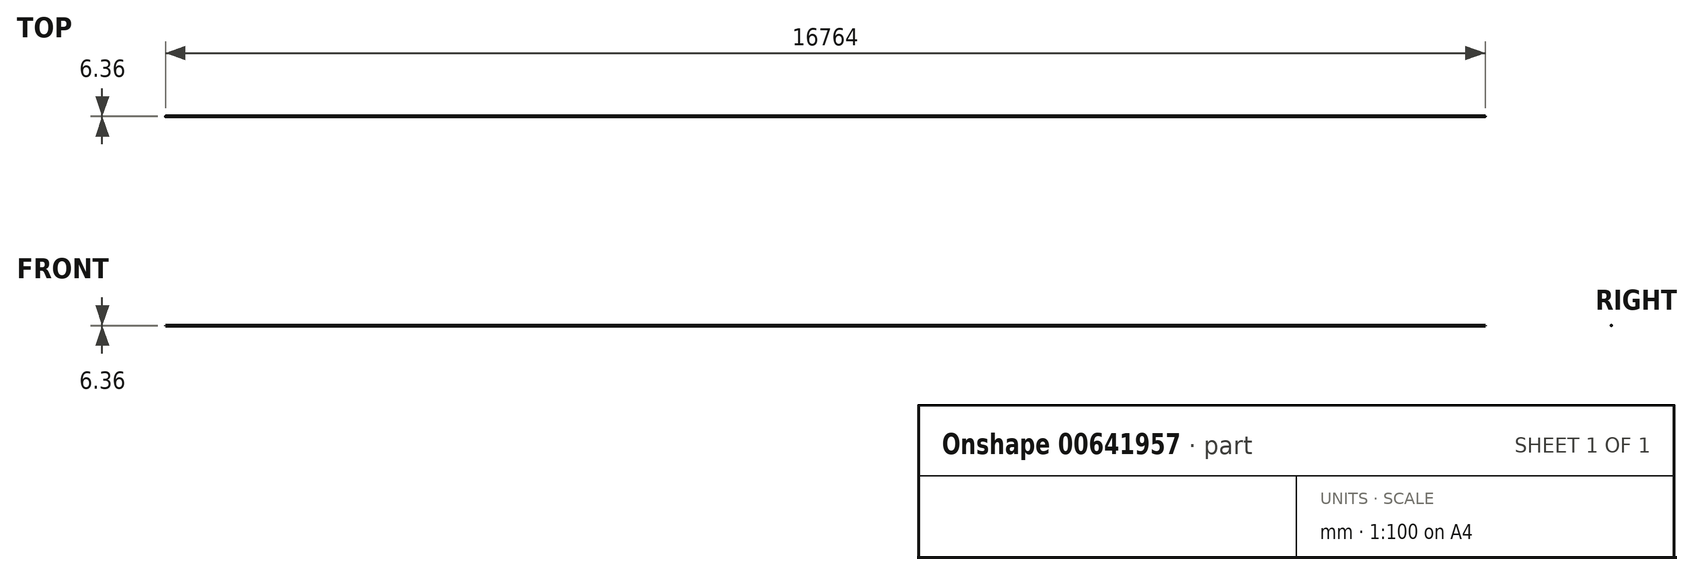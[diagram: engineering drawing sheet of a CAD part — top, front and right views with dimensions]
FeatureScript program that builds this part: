
annotation { "Feature Type Name" : "Feature", "Feature Type Description" : "" }
export const myFeature = defineFeature(function(context is Context, id is Id, definition is map)
    precondition{}
    {
        {
            var Q0;
            Q0=qCreatedBy(makeId("Right.planeOp"),FACE);
            var sketch = newSketch(context, id + "F0", { "sketchPlane" : qUnion([Q0])});
            skCircle(sketch, "E0", {"center": v(0, 0) * mm, "radius": 3.18 * mm});
            skSolve(sketch);
        }
        {
            var Q0;
            Q0 = qSketchRegion(id + "F0", true);
            extrude(context, id + "F1", {"entities" : qUnion([Q0]), "oppositeDirection" : true, "depth" : 16764 * mm, "offsetDistance" : 30.48 * mm});
        }
    });
